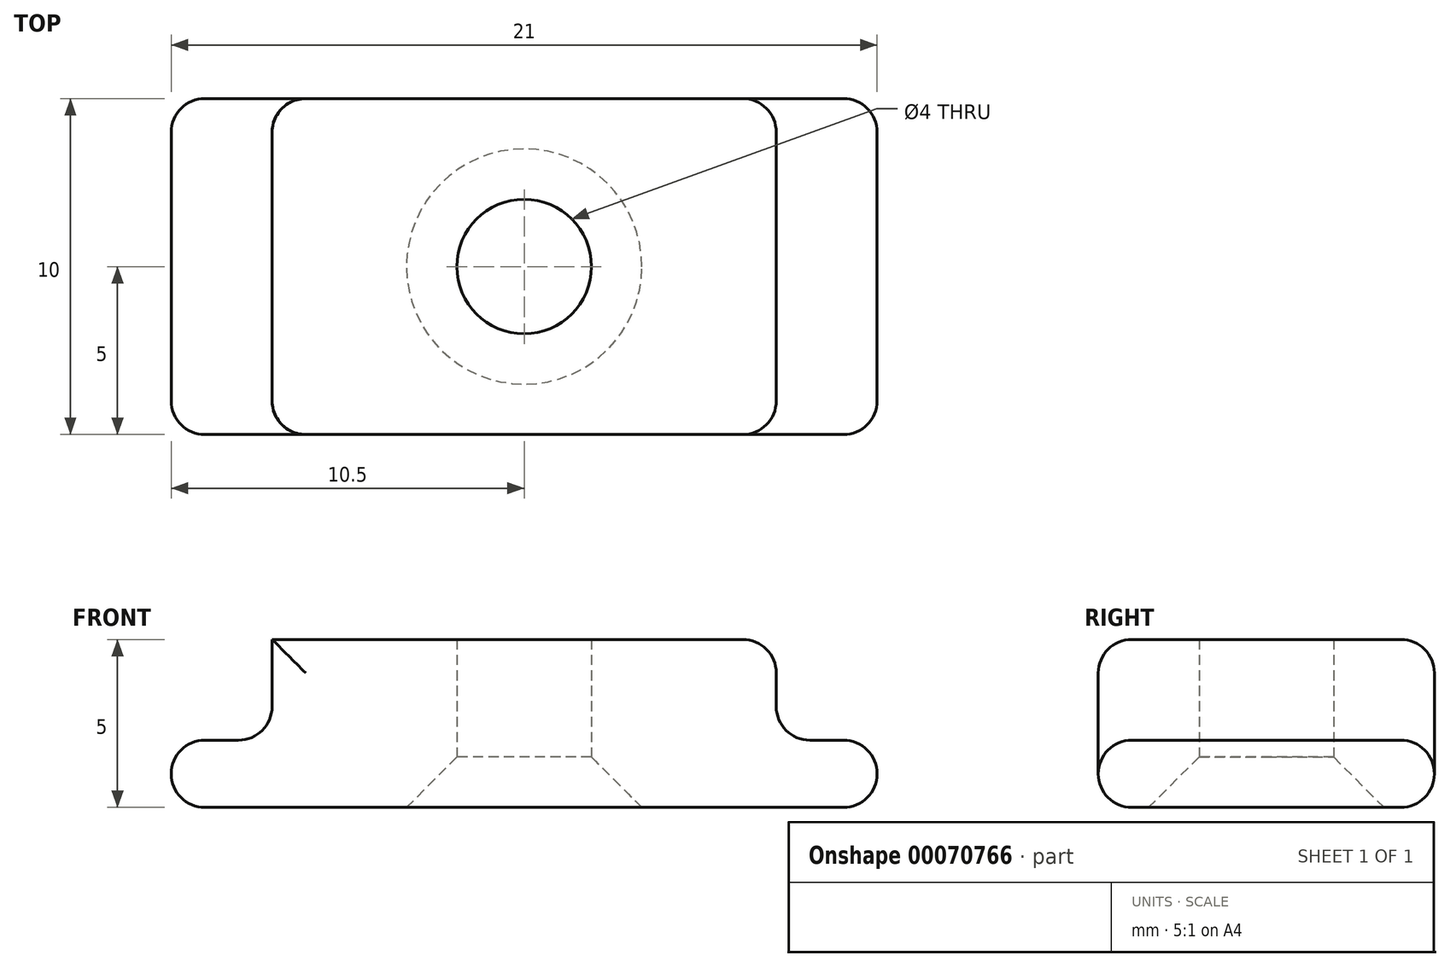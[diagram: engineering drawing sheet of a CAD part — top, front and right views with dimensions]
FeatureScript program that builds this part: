
annotation { "Feature Type Name" : "Feature", "Feature Type Description" : "" }
export const myFeature = defineFeature(function(context is Context, id is Id, definition is map)
    precondition{}
    {
        {
            var Q0;
            Q0=qCreatedBy(makeId("Top.planeOp"),FACE);
            var sketch = newSketch(context, id + "F0", { "sketchPlane" : qUnion([Q0])});
            skLineSegment(sketch, "E0.bottom", {"start": v(0, 0) * mm, "end": v(15, 0) * mm});
            skLineSegment(sketch, "E0.top", {"start": v(0, -10) * mm, "end": v(15, -10) * mm});
            skLineSegment(sketch, "E0.left", {"start": v(0, 0) * mm, "end": v(0, -10) * mm});
            skLineSegment(sketch, "E0.right", {"start": v(15, 0) * mm, "end": v(15, -10) * mm});
            skLineSegment(sketch, "E1.bottom", {"start": v(0, -10) * mm, "end": v(-3, -10) * mm});
            skLineSegment(sketch, "E1.top", {"start": v(0, 0) * mm, "end": v(-3, 0) * mm});
            skLineSegment(sketch, "E1.left", {"start": v(0, -10) * mm, "end": v(0, 0) * mm});
            skLineSegment(sketch, "E1.right", {"start": v(-3, -10) * mm, "end": v(-3, 0) * mm});
            skLineSegment(sketch, "E2.bottom", {"start": v(15, 0) * mm, "end": v(18, 0) * mm});
            skLineSegment(sketch, "E2.top", {"start": v(15, -10) * mm, "end": v(18, -10) * mm});
            skLineSegment(sketch, "E2.right", {"start": v(18, 0) * mm, "end": v(18, -10) * mm});
            skCircle(sketch, "E3", {"center": v(7.5, -5) * mm, "radius": 2 * mm});
            skLineSegment(sketch, "E4", {"start": v(0, -5) * mm, "end": v(15, -5) * mm, "construction": true});
            skLineSegment(sketch, "E5", {"start": v(7.5, 0) * mm, "end": v(7.5, -10) * mm, "construction": true});
            skCircle(sketch, "E6", {"center": v(7.5, -5) * mm, "radius": 3.5 * mm});
            skSolve(sketch);
        }
        {
            var Q0;
            Q0=makeQuery(id+"F0.imprint","IMPRINT",FACE,{"disambiguationData":[TD([[makeQuery(id+"F0.imprint","IMPRINT",EDGE,{"derivedFrom":sQuery(id+"F0.wireOp",EDGE,"E0.bottom")}),-1.0]])]});
            extrude(context, id + "F1", {"entities" : qUnion([Q0]), "depth" : 5 * mm});
        }
        {
            var Q0;
            Q0=makeQuery(id+"F0.imprint","IMPRINT",FACE,{"disambiguationData":[TD([[makeQuery(id+"F0.imprint","IMPRINT",EDGE,{"derivedFrom":sQuery(id+"F0.wireOp",EDGE,"E1.bottom")}),-1.0]])]});
            var Q1;
            Q1=makeQuery(id+"F0.imprint","IMPRINT",FACE,{"disambiguationData":[TD([[makeQuery(id+"F0.imprint","IMPRINT",EDGE,{"derivedFrom":sQuery(id+"F0.wireOp",EDGE,"E2.bottom")}),-1.0]])]});
            extrude(context, id + "F2", {"entities" : qUnion([Q0, Q1]), "operationType" : NewBodyOperationType.ADD, "depth" : 2 * mm});
        }
        {
            var Q0;
            Q0=makeQuery(id+"F2.boolean.opBoolean","MERGE",FACE,{"derivedFrom":[makeQuery(id+"F1.opExtrude","SWEPT_FACE",FACE,{"disambiguationData":[OSD([sQuery(id+"F0.wireOp",EDGE,"E0.bottom")])]}),makeQuery(id+"F2.opExtrude","SWEPT_FACE",FACE,{"disambiguationData":[OSD([sQuery(id+"F0.wireOp",EDGE,"E1.top")])]}),makeQuery(id+"F2.opExtrude","SWEPT_FACE",FACE,{"disambiguationData":[OSD([sQuery(id+"F0.wireOp",EDGE,"E2.bottom")])]})]});
            var Q1;
            Q1=makeQuery(id+"F2.boolean.opBoolean","MERGE",FACE,{"derivedFrom":[makeQuery(id+"F1.opExtrude","SWEPT_FACE",FACE,{"disambiguationData":[OSD([sQuery(id+"F0.wireOp",EDGE,"E0.top")])]}),makeQuery(id+"F2.opExtrude","SWEPT_FACE",FACE,{"disambiguationData":[OSD([sQuery(id+"F0.wireOp",EDGE,"E1.bottom")])]}),makeQuery(id+"F2.opExtrude","SWEPT_FACE",FACE,{"disambiguationData":[OSD([sQuery(id+"F0.wireOp",EDGE,"E2.top")])]})]});
            var Q2;
            Q2=makeQuery(id+"F1.opExtrude","SWEPT_FACE",FACE,{"disambiguationData":[OSD([sQuery(id+"F0.wireOp",EDGE,"E0.right")])]});
            var Q3;
            Q3=makeQuery(id+"F2.opExtrude","SWEPT_FACE",FACE,{"disambiguationData":[OSD([sQuery(id+"F0.wireOp",EDGE,"E2.right")])]});
            var Q4;
            Q4=makeQuery(id+"F2.opExtrude","CAP_FACE",FACE,{"disambiguationData":[OSD([sQuery(id+"F0.wireOp",EDGE,"E2.bottom"),sQuery(id+"F0.wireOp",EDGE,"E2.top"),sQuery(id+"F0.wireOp",EDGE,"E0.right"),sQuery(id+"F0.wireOp",EDGE,"E2.right")])],"isStart":false});
            var Q5;
            Q5=makeQuery(id+"F2.opExtrude","CAP_FACE",FACE,{"disambiguationData":[OSD([sQuery(id+"F0.wireOp",EDGE,"E1.bottom"),sQuery(id+"F0.wireOp",EDGE,"E1.top"),sQuery(id+"F0.wireOp",EDGE,"E1.left"),sQuery(id+"F0.wireOp",EDGE,"E1.right")])],"isStart":false});
            var Q6;
            Q6=makeQuery(id+"F1.opExtrude","SWEPT_FACE",FACE,{"disambiguationData":[OSD([sQuery(id+"F0.wireOp",EDGE,"E1.left")])]});
            var Q7;
            Q7=makeQuery(id+"F2.opExtrude","SWEPT_FACE",FACE,{"disambiguationData":[OSD([sQuery(id+"F0.wireOp",EDGE,"E1.right")])]});
            fillet(context, id + "F3", {"entities" : qUnion([Q0, Q1, Q2, Q3, Q4, Q5, Q6, Q7]), "radius" : 1 * mm, "tangentPropagation" : true, "allowEdgeOverflow" : false});
        }
        {
            var Q0;
            Q0=makeQuery(id+"F0.imprint","IMPRINT",FACE,{"disambiguationData":[TD([[makeQuery(id+"F0.imprint","IMPRINT",EDGE,{"derivedFrom":sQuery(id+"F0.wireOp",EDGE,"E3")}),-1.0]])]});
            extrude(context, id + "F4", {"entities" : qUnion([Q0]), "operationType" : NewBodyOperationType.ADD, "depth" : 5 * mm});
        }
        {
            var Q0;
            Q0=makeQuery(id+"F4.opExtrude","CAP_EDGE",EDGE,{"disambiguationData":[OSD([sQuery(id+"F0.wireOp",EDGE,"E3")])],"isStart":true});
            chamfer(context, id + "F5", {"entities" : qUnion([Q0]), "width" : 1.5 * mm, "tangentPropagation" : true});
        }
    });
